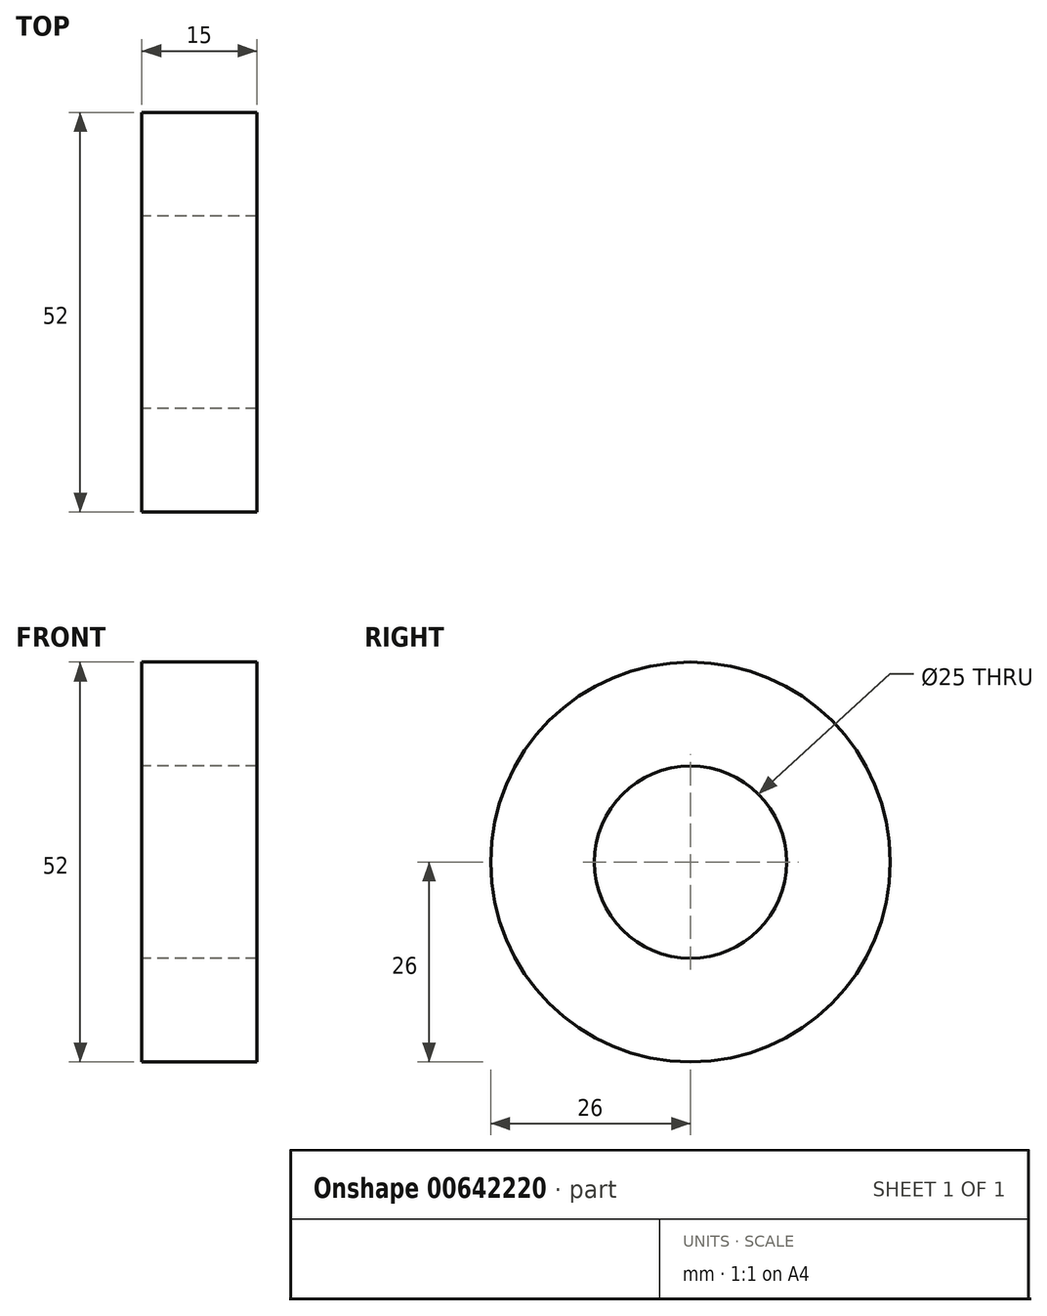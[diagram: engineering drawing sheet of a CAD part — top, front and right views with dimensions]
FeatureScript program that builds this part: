
annotation { "Feature Type Name" : "Feature", "Feature Type Description" : "" }
export const myFeature = defineFeature(function(context is Context, id is Id, definition is map)
    precondition{}
    {
        {
            var Q0;
            Q0=qCreatedBy(makeId("Front.planeOp"),FACE);
            var sketch = newSketch(context, id + "F0", { "sketchPlane" : qUnion([Q0])});
            skLineSegment(sketch, "E0.bottom", {"start": v(15, 12.5) * mm, "end": v(0, 12.5) * mm});
            skLineSegment(sketch, "E0.top", {"start": v(15, 26) * mm, "end": v(0, 26) * mm});
            skLineSegment(sketch, "E0.left", {"start": v(15, 12.5) * mm, "end": v(15, 26) * mm});
            skLineSegment(sketch, "E0.right", {"start": v(0, 12.5) * mm, "end": v(0, 26) * mm});
            skLineSegment(sketch, "E1", {"start": v(0, 0) * mm, "end": v(7.5, 0) * mm, "construction": true});
            skSolve(sketch);
        }
        {
            var Q0;
            Q0=qSketchRegion(id+"F0",true);
            var Q1;
            Q1=sQuery(id+"F0.wireOp",EDGE,"E1");
            revolve(context, id + "F1", {"entities" : qUnion([Q0]), "axis" : qUnion([Q1]), "revolveType" : RevolveType.FULL});
        }
    });
